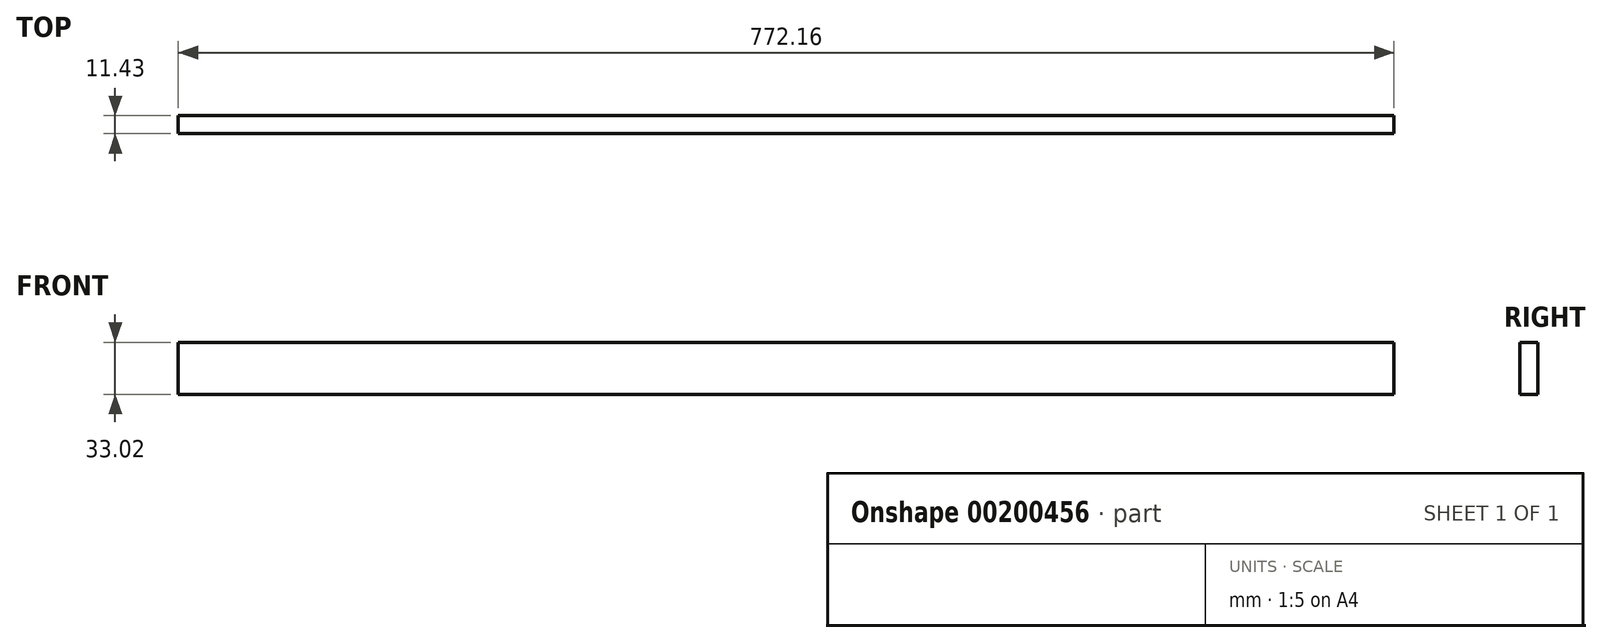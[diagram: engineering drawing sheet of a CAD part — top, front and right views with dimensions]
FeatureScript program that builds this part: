
annotation { "Feature Type Name" : "Feature", "Feature Type Description" : "" }
export const myFeature = defineFeature(function(context is Context, id is Id, definition is map)
    precondition{}
    {
        {
            var Q0;
            Q0=qCreatedBy(makeId("Front.planeOp"),FACE);
            var sketch = newSketch(context, id + "F0", { "sketchPlane" : qUnion([Q0])});
            skLineSegment(sketch, "E0.bottom", {"start": v(-1014.38, -127.15) * mm, "end": v(-242.22, -127.15) * mm});
            skLineSegment(sketch, "E0.top", {"start": v(-1014.38, -160.17) * mm, "end": v(-242.22, -160.17) * mm});
            skLineSegment(sketch, "E0.left", {"start": v(-1014.38, -127.15) * mm, "end": v(-1014.38, -160.17) * mm});
            skLineSegment(sketch, "E0.right", {"start": v(-242.22, -127.15) * mm, "end": v(-242.22, -160.17) * mm});
            skSolve(sketch);
        }
        {
            var Q0;
            Q0 = qSketchRegion(id + "F0", true);
            extrude(context, id + "F1", {"entities" : qUnion([Q0]), "depth" : 11.43 * mm});
        }
    });
